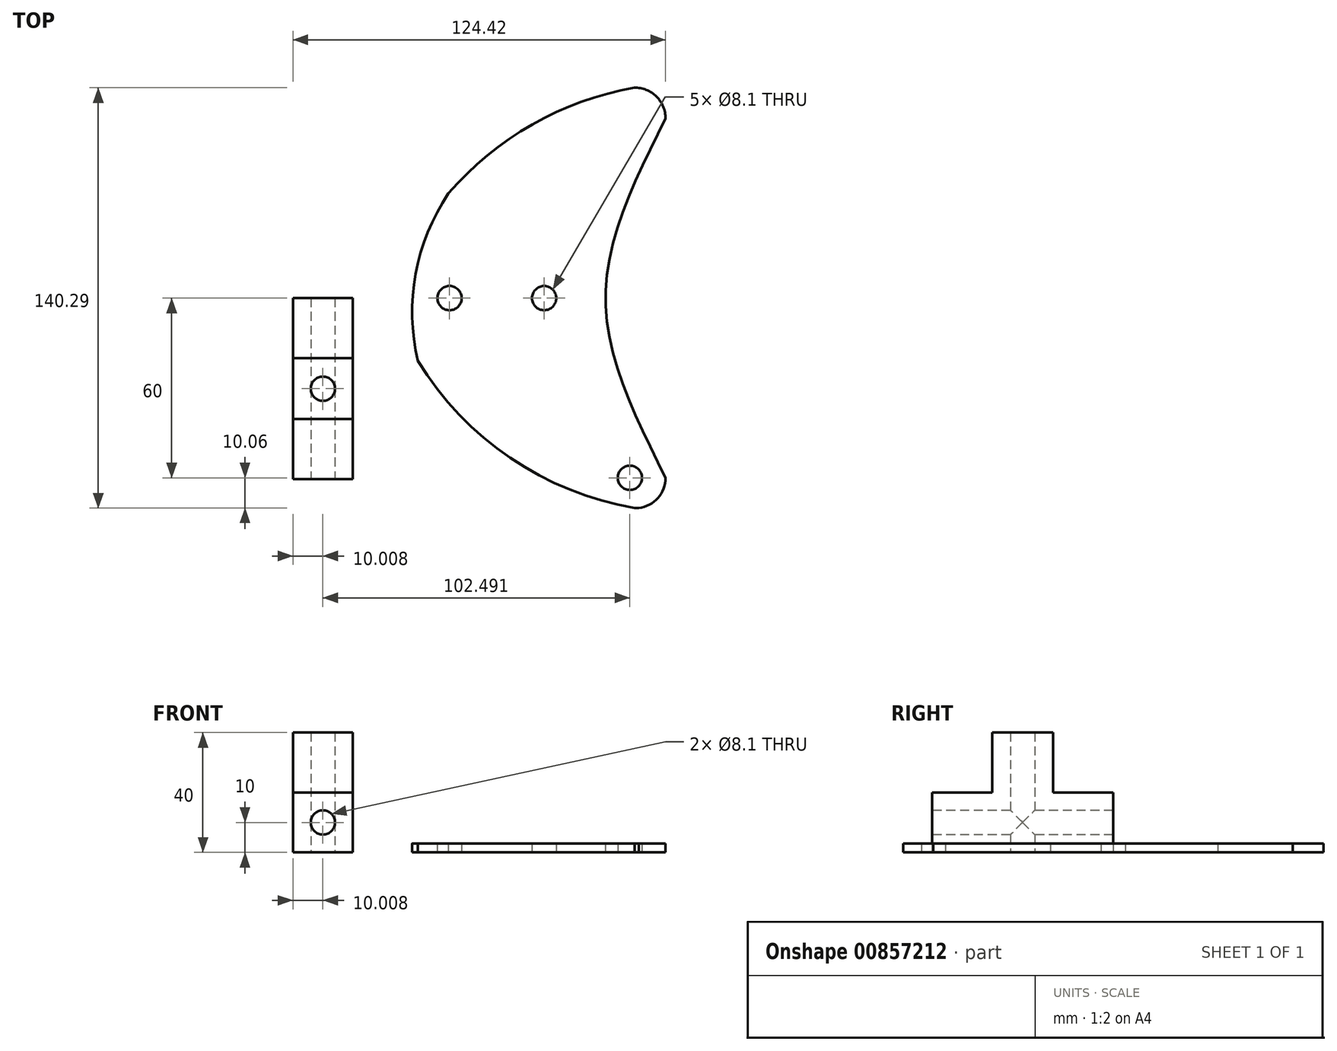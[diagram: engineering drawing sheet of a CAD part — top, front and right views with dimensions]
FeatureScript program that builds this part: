
annotation { "Feature Type Name" : "Feature", "Feature Type Description" : "" }
export const myFeature = defineFeature(function(context is Context, id is Id, definition is map)
    precondition{}
    {
        {
            var Q0;
            Q0=qCreatedBy(makeId("Top.planeOp"),FACE);
            var sketch = newSketch(context, id + "F0", { "sketchPlane" : qUnion([Q0])});
            skPoint(sketch, "E0.middle", {"position": v(0, 0) * mm});
            skFitSpline(sketch, "E1", {"points": [v(46.25, 60) * mm, v(26.22, 0) * mm, v(46.25, -60) * mm], "startDerivative": vector(-60.1, -120) * mm, "endDerivative": vector(60.1, -120) * mm});
            skArc(sketch, "E2", {"start": v(46.25, 60) * mm, "mid": v(43.18, 67.3) * mm, "end": v(35.82, 70.23) * mm});
            skArc(sketch, "E3", {"start": v(37.3, -70.06) * mm, "mid": v(43.7, -66.73) * mm, "end": v(46.25, -60) * mm});
            skArc(sketch, "E4", {"start": v(35.82, 70.23) * mm, "mid": v(-14.81, 46.33) * mm, "end": v(-46.25, 0) * mm});
            skArc(sketch, "E5", {"start": v(-46.25, 0) * mm, "mid": v(-14.77, -46.34) * mm, "end": v(35.98, -70.06) * mm});
            skPoint(sketch, "E6", {"position": v(-25.9, 0) * mm});
            skPoint(sketch, "E7", {"position": v(5.7, 0) * mm});
            skPoint(sketch, "E8", {"position": v(34.33, -60) * mm});
            skLineSegment(sketch, "E9", {"start": v(35.98, -70.06) * mm, "end": v(37.3, -70.06) * mm});
            skArc(sketch, "E10", {"start": v(-26.25, 34.93) * mm, "mid": v(-37.19, 8.05) * mm, "end": v(-36.44, -20.95) * mm});
            skLineSegment(sketch, "E11.bottom", {"start": v(-58.15, 0) * mm, "end": v(-78.17, 0) * mm});
            skLineSegment(sketch, "E11.top", {"start": v(-58.15, -60.47) * mm, "end": v(-78.17, -60.47) * mm});
            skLineSegment(sketch, "E11.left", {"start": v(-58.15, 0) * mm, "end": v(-58.15, -60.47) * mm});
            skLineSegment(sketch, "E11.right", {"start": v(-78.17, 0) * mm, "end": v(-78.17, -60.47) * mm});
            skLineSegment(sketch, "E12.bottom", {"start": v(-78.17, 0) * mm, "end": v(-58.15, 0) * mm});
            skLineSegment(sketch, "E12.left", {"start": v(-78.17, 0) * mm, "end": v(-78.17, -30.23) * mm});
            skLineSegment(sketch, "E12.right", {"start": v(-58.15, 0) * mm, "end": v(-58.15, -30.23) * mm});
            skPoint(sketch, "E13", {"position": v(-68.16, -30.23) * mm});
            skLineSegment(sketch, "E14.bottom", {"start": v(-78.17, -20.1) * mm, "end": v(-58.15, -20.1) * mm});
            skLineSegment(sketch, "E14.top", {"start": v(-78.17, -40.37) * mm, "end": v(-58.15, -40.37) * mm});
            skLineSegment(sketch, "E14.left", {"start": v(-78.17, -20.1) * mm, "end": v(-78.17, -40.37) * mm});
            skLineSegment(sketch, "E14.right", {"start": v(-58.15, -20.1) * mm, "end": v(-58.15, -40.37) * mm});
            skSolve(sketch);
        }
        {
            var Q0;
            Q0=makeQuery(id+"F0.imprint","IMPRINT",FACE,{"disambiguationData":[TD([[makeQuery(id+"F0.imprint","IMPRINT",EDGE,{"derivedFrom":sQuery(id+"F0.wireOp",EDGE,"E1")}),-1.0]])]});
            extrude(context, id + "F1", {"entities" : qUnion([Q0]), "depth" : 3 * mm, "offsetDistance" : 25 * mm});
        }
        {
            var Q0;
            Q0=sQuery(id+"F0.wireOp",VERTEX,"E8");
            var Q1;
            Q1=sQuery(id+"F0.wireOp",VERTEX,"E7");
            var Q2;
            Q2=sQuery(id+"F0.wireOp",VERTEX,"E6");
            var Q3;
            Q3=makeQuery(id+"F1.opExtrude","SWEPT_BODY",BODY,{"disambiguationData":[OSD([sQuery(id+"F0.wireOp",EDGE,"E1"),sQuery(id+"F0.wireOp",EDGE,"E2"),sQuery(id+"F0.wireOp",EDGE,"E3"),sQuery(id+"F0.wireOp",EDGE,"E4"),sQuery(id+"F0.wireOp",EDGE,"E5"),sQuery(id+"F0.wireOp",EDGE,"E9")])]});
            hole(context, id + "F2", {"style" : HoleStyle.SIMPLE, "endStyle" : HoleEndStyle.THROUGH, "oppositeDirection" : true, "holeDiameter" : 8.1 * mm, "majorDiameter" : 5 * mm, "isTappedThrough" : true, "tappedDepth" : 12 * mm, "tapClearance" : 3, "startFromSketch" : true, "locations" : qUnion([Q0, Q1, Q2]), "scope" : qUnion([Q3])});
        }
        {
            var Q0;
            Q0=makeQuery(id+"F0.imprint","IMPRINT",FACE,{"disambiguationData":[TD([[makeQuery(id+"F0.imprint","IMPRINT",EDGE,{"derivedFrom":sQuery(id+"F0.wireOp",EDGE,"E11.bottom")}),1.0]])]});
            var Q1;
            {var subQ0=sQuery(id+"F0.wireOp",EDGE,"E14.bottom");Q1=makeQuery(id+"F0.imprint","IMPRINT",FACE,{"disambiguationData":[TD([[makeQuery(id+"F0.imprint","IMPRINT",EDGE,{"derivedFrom":subQ0}),-1.0]])]});}
            var Q2;
            Q2=makeQuery(id+"F0.imprint","IMPRINT",FACE,{"disambiguationData":[TD([[makeQuery(id+"F0.imprint","IMPRINT",EDGE,{"derivedFrom":sQuery(id+"F0.wireOp",EDGE,"E12.bottom")}),-1.0]])]});
            var Q3;
            Q3=makeQuery(id+"F0.imprint","IMPRINT",FACE,{"disambiguationData":[TD([[makeQuery(id+"F0.imprint","IMPRINT",EDGE,{"derivedFrom":sQuery(id+"F0.wireOp",EDGE,"E11.top")}),-1.0]])]});
            extrude(context, id + "F3", {"entities" : qUnion([Q0, Q1, Q2, Q3]), "depth" : 20 * mm, "offsetDistance" : 25 * mm});
        }
        {
            var Q0;
            {var subQ0=sQuery(id+"F0.wireOp",EDGE,"E14.bottom");Q0=makeQuery(id+"F0.imprint","IMPRINT",FACE,{"disambiguationData":[TD([[makeQuery(id+"F0.imprint","IMPRINT",EDGE,{"derivedFrom":subQ0}),-1.0]])]});}
            extrude(context, id + "F4", {"entities" : qUnion([Q0]), "operationType" : NewBodyOperationType.ADD, "depth" : 40 * mm, "offsetDistance" : 25 * mm});
        }
        {
            var Q0;
            Q0=sQuery(id+"F0.wireOp",VERTEX,"E13");
            var Q1;
            Q1=makeQuery(id+"F3.opExtrude","SWEPT_BODY",BODY,{"disambiguationData":[OSD([sQuery(id+"F0.wireOp",EDGE,"E11.top"),sQuery(id+"F0.wireOp",EDGE,"E11.left"),sQuery(id+"F0.wireOp",EDGE,"E11.right"),sQuery(id+"F0.wireOp",EDGE,"E12.bottom"),sQuery(id+"F0.wireOp",EDGE,"E12.left"),sQuery(id+"F0.wireOp",EDGE,"E12.right"),sQuery(id+"F0.wireOp",EDGE,"E14.left"),sQuery(id+"F0.wireOp",EDGE,"E14.right")])]});
            hole(context, id + "F5", {"style" : HoleStyle.SIMPLE, "endStyle" : HoleEndStyle.THROUGH, "oppositeDirection" : true, "holeDiameter" : 8.1 * mm, "majorDiameter" : 5 * mm, "isTappedThrough" : true, "tappedDepth" : 12 * mm, "tapClearance" : 3, "startFromSketch" : true, "locations" : qUnion([Q0]), "scope" : qUnion([Q1])});
        }
        {
            var Q0;
            Q0=makeQuery(id+"F3.opExtrude","SWEPT_FACE",FACE,{"disambiguationData":[OSD([sQuery(id+"F0.wireOp",EDGE,"E11.top")])]});
            var sketch = newSketch(context, id + "F6", { "sketchPlane" : qUnion([Q0])});
            skLineSegment(sketch, "E15.bottom", {"start": v(-78.17, 20) * mm, "end": v(-58.15, 20) * mm});
            skLineSegment(sketch, "E15.top", {"start": v(-78.17, 0) * mm, "end": v(-58.15, 0) * mm});
            skLineSegment(sketch, "E15.left", {"start": v(-78.17, 20) * mm, "end": v(-78.17, 0) * mm});
            skLineSegment(sketch, "E15.right", {"start": v(-58.15, 20) * mm, "end": v(-58.15, 0) * mm});
            skLineSegment(sketch, "E16", {"start": v(-58.15, 10) * mm, "end": v(-78.17, 10) * mm});
            skPoint(sketch, "E17", {"position": v(-68.16, 10) * mm});
            skSolve(sketch);
        }
        {
            var Q0;
            Q0=sQuery(id+"F6.wireOp",VERTEX,"E17");
            var Q1;
            Q1=makeQuery(id+"F3.opExtrude","SWEPT_BODY",BODY,{"disambiguationData":[OSD([sQuery(id+"F0.wireOp",EDGE,"E11.top"),sQuery(id+"F0.wireOp",EDGE,"E11.left"),sQuery(id+"F0.wireOp",EDGE,"E11.right"),sQuery(id+"F0.wireOp",EDGE,"E12.bottom"),sQuery(id+"F0.wireOp",EDGE,"E12.left"),sQuery(id+"F0.wireOp",EDGE,"E12.right"),sQuery(id+"F0.wireOp",EDGE,"E14.left"),sQuery(id+"F0.wireOp",EDGE,"E14.right")])]});
            hole(context, id + "F7", {"style" : HoleStyle.SIMPLE, "endStyle" : HoleEndStyle.THROUGH, "holeDiameter" : 8.1 * mm, "majorDiameter" : 5 * mm, "isTappedThrough" : true, "tappedDepth" : 12 * mm, "tapClearance" : 3, "startFromSketch" : true, "locations" : qUnion([Q0]), "scope" : qUnion([Q1])});
        }
    });
